# Revit family: IS_Ceraplan_BD228_BIM_NL
name_source: partatom
category: Plumbing Fixtures
units: mm (PartAtom-declared; Revit-internal decimal feet)

## family parameters
Always vertical = No
Cut with Voids When Loaded = No
OmniClass Number = 23.45.55.17
OmniClass Title = Mixing Faucets
Part Type = Normal
Room Calculation Point = No
Round Connector Dimension = Use Diameter
Shared = No
Work Plane-Based = No

## types (2) — shared parameters
Accessories = https://www.idealstandard.nl
Afmetingen = 49 x 193 x 161 mm
AfstandsEenheid = Millimeter
AreaUnits = millimeter
Artikelomschrijving = CERAPLAN WASCHTISCHMISCHER H90 RTD BLUE START , METALL POP-UP ABFALL, 5L.
Artikelreferentie = CERAPLAN BASIN MIXER H90 RTD BLUE START , METAL POP-UP WASTE, 5L.
Auteur = Ideal Standard
BIMObjectName = IS_IdealStandard_Washbasintaps_Ceraplan_BD228
BIMobject category = Sanitary
BIMobject main category = Taps & Mixers
Bedieningkraan = manueller Einhebelmischer
Bedieningkraanwerk = Einhebel
Beschrijvinggarantie = Herstellergarantie
Bestanddelen = WASCHTISCHMISCHER H90 RTD BLUE START , METALL POP-UP ABFALL, 5L.
BimObjectNaam = IS_IdealStandard_Washbasintaps_Ceraplan_BD228
Brand = Ideal Standard
Brand url = http://www.idealstandard.nl
Breedte = 48.73946
ConnectionType = Plumbing
CurrencyUnit = €
CurrentRevision = 1
Date of publishing = 17/09/2021
Description = CERAPLAN BASIN MIXER H90 RTD BLUE START , METAL POP-UP WASTE, 5L.
Diepte = 193 mm
Douchebak = No
DurationUnit = Years
DuurEenheid = Bar
Edition number = 1
Eigenschappen = WASCHTISCHMISCHER H90 RTD BLUE START , METALL POP-UP ABFALL, 5L.
ElementType = 5
FaucetFunction = Mixer
FaucetOperation = Single Lever Handle
FaucetTopDescription = Single Lever Handle
FaucetType = Basin Single Lever Mixer
Features = BASIN MIXER H90 RTD BLUE START , METAL POP-UP WASTE, 5L.
Functiekraanwerk = Waschtischmischer
Garantieonderdelen = 5
Garantieunits = Jaren
Help = https://www.idealstandard.nl
Hoogte = 161.311142311606
Hulp = https://www.idealstandard.nl
IFC Classification = Sanitary Terminal
IfcExportAs = IfcValveType
IfcExportType = MIXING
Installatieinstructies = https://www.idealstandard.nl
Installation instructions = https://www.idealstandard.nl
InstallationInstructions = https://www.idealstandard.nl
IsBuiltIn = No
IsHighPressure = No
Klepmechanisme = enkele hendel
LinearUnits = Millimetres
MaintenanceInformation = https://www.idealstandard.nl
Manufacturer = Ideal Standard
Manufacturer name = Ideal Standard
ManufacturerURL = https://www.idealstandard.nl
Masterformat 2014 Code = 22 41 39
Masterformat 2014 Description = Residential Faucets, Supplies, and Trim
Materiaal = Messing
Material = Brass
Material main = Brass
Merk = Ideal Standard
ModelNumber = BD228
ModelReference = CERAPLAN BASIN MIXER H90 RTD BLUE START , METAL POP-UP WASTE, 5L.
Montageinstuctie = https://www.idealstandard.nl
NBS Reference Code = 45-35-70/371
NBS Reference Description = Water supply fittings for wash basins and troughs
Name = Washbasintaps_Ceraplan_BD228_IdealStandard
NettWeight = 1,71 KG
NominalDepth = 193 mm
NominalHeight = 161 mm
NominalLength = 193 mm
NominalWidth = 49 mm  [stored 0.160761 ft]
OmniClass Code = 23-31 11 00
OmniClass Description = Fauces
OppervlakteEenheid = millimeter
Product Guid = dc0b2742-77a0-41fc-9ac3-17f03cb89bbc
Product SKU = BD228
Product certification = https://www.idealstandard.nl
Product data url = https://bimobject.com
Product family = Sanitary
Product group = Mixers & Taps
Product name = CERAPLAN BASIN MIXER H90 RTD BLUE START , METAL POP-UP WASTE, 5L
Product url = https://www.idealstandard.nl
ProductInformation = https://www.idealstandard.nl
Productinformatie = https://www.idealstandard.nl
QR code = http://bimobject.com
Revisie = 1
Shape = Cylindrical
Size = 49 x 193 x 161 mm
Space = Internal
SpareParts = https://www.idealstandard.nl
Technical description = https://www.idealstandard.nl
Telefoonnummer = 077 355 08 08
TestPressure = 10 bar
Testdruk = 10 bar
Typekraanwerk = Einhebel
UNSPSC Code = 301815
URL = https://www.idealstandard.nl
Uniclass 1.4 Code = L725111
Uniclass 1.4 Description = Mixer taps
Uniclass 2.0 Code = PR-35-79-85
Uniclass 2.0 Description = Wash Basin and Trough Water Supply Fittings
Uniclass 2015 Code = Pr_40_20_87_98
Uniclass 2015 Name = Washbasin taps
Uniclass2015Beschrijving = Washbasin taps
Uniclass2015Code = Pr_40_20_87_98
Uniclass2015Referentie = Pr_40_20_87_98
Uniclass2015Title = Washbasin taps
Uniclass2015Version = v1.22
Urlproducent = https://www.idealstandard.nl
ValutaEenheid = Euro
ValveMechanism = Mixer
ValveOperation = Single Lever
Versie = 1
Version = 1
VolumeUnits = Litres
Volumeunits = Liter
Vorm = Zylinder
WRASURL = https://www.wrasapprovals.co.uk
WarrantyDescription = Manufacturer Warranty
WarrantyDurationParts = 5
WarrantyDurationUnit = Years
Wisselstukken = https://www.idealstandard.nl
Youtube clip = https://www.youtube.com
zero-valued in all types: BrutoGewicht, Cost, Default Elevation, GrootteAfvoergat, InletConnectionSize, Lengte, Nettogewicht, Overloop, SpilloverLevel, Vervangingskosten

## per-type parameters (varying)
| type | Afwerking | Artikelnummer | BarCode | Color | Finish | GTIN code | Kleur | MainColor | Model |
| BD228AA - CERAPLAN BASIN MIXER H90 RTD BLUE START , METAL POP-UP WASTE, 5L - CHROME | Chrom | BD228AA | 3800861103691 | Chrome | Chrome | 3800861103691 | Chrom | Silk Black | BD228AA |
| BD228XG - CERAPLAN BASIN MIXER H90 RTD BLUE START , METAL POP-UP WASTE, 5L - SILK BLACK | Seidenschwarz | BD228XG | 3800861116790 | Silk Black | Silk Black | 3800861116790 | Seidenschwarz | Chrome | BD228XG |

note: [stored X ft] marks values corroborated as IEEE doubles in the binary element streams (Revit-internal decimal feet)

## geometry (parser evidence)
native form markers: Blend x2, Sweep x3
no freeform markers — native parametric forms only
